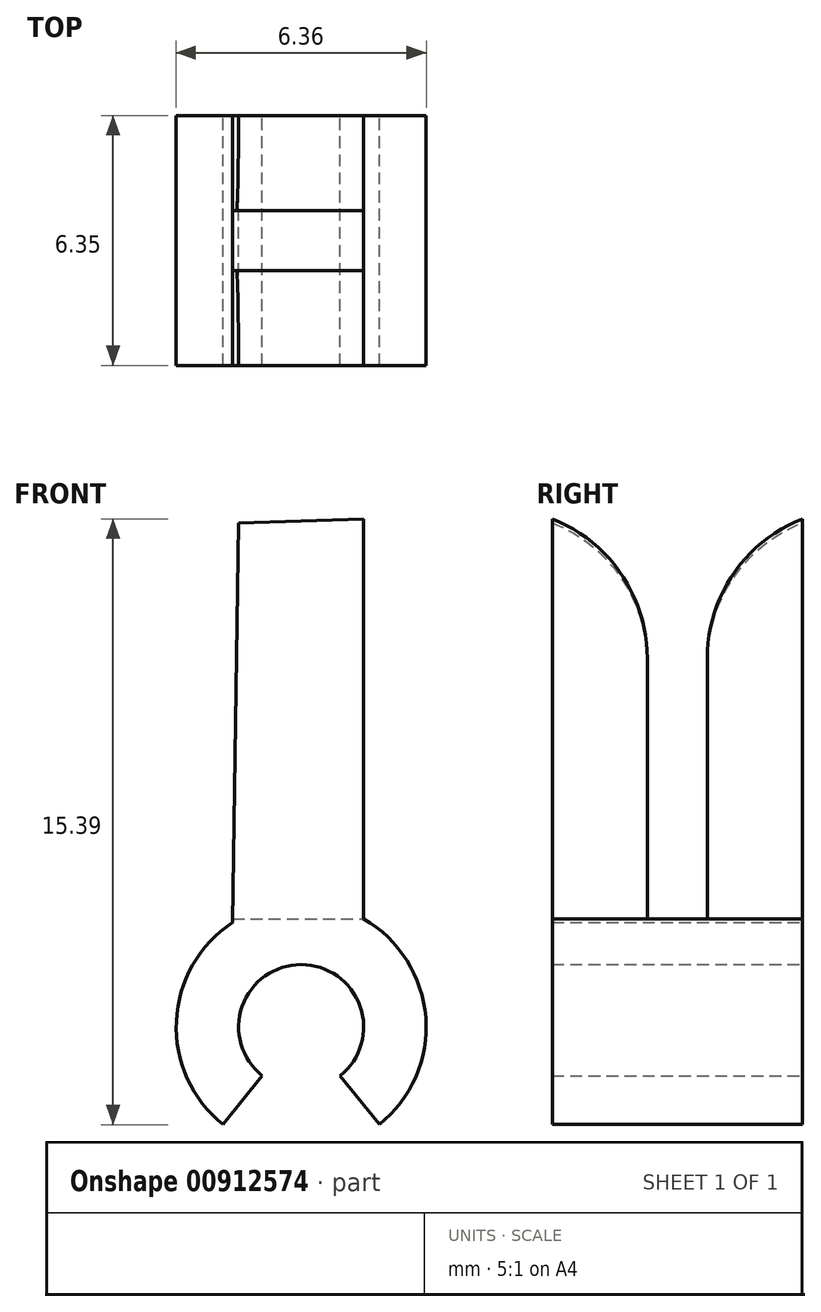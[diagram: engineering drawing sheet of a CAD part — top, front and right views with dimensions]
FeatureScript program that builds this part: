
annotation { "Feature Type Name" : "Feature", "Feature Type Description" : "" }
export const myFeature = defineFeature(function(context is Context, id is Id, definition is map)
    precondition{}
    {
        {
            var Q0;
            Q0=qCreatedBy(makeId("Front.planeOp"),FACE);
            var sketch = newSketch(context, id + "F0", { "sketchPlane" : qUnion([Q0])});
            skArc(sketch, "E0", {"start": v(1.99, -2.48) * mm, "mid": v(3.17, 0.24) * mm, "end": v(1.59, 2.75) * mm});
            skArc(sketch, "E1", {"start": v(1, -1.24) * mm, "mid": v(0, 1.59) * mm, "end": v(-1, -1.24) * mm});
            skLineSegment(sketch, "E2", {"start": v(-1, -1.24) * mm, "end": v(-1.99, -2.48) * mm});
            skLineSegment(sketch, "E3", {"start": v(1, -1.24) * mm, "end": v(1.99, -2.48) * mm});
            skArc(sketch, "E4.trimOffspring", {"start": v(-1.74, 2.65) * mm, "mid": v(-3.17, 0.15) * mm, "end": v(-1.99, -2.48) * mm});
            skLineSegment(sketch, "E5.left", {"start": v(-1.74, 2.65) * mm, "end": v(-1.59, 12.81) * mm});
            skLineSegment(sketch, "E6", {"start": v(-1.59, 12.81) * mm, "end": v(1.59, 12.9) * mm});
            skLineSegment(sketch, "E7", {"start": v(1.59, 12.9) * mm, "end": v(1.59, 2.75) * mm});
            skSolve(sketch);
        }
        {
            var Q0;
            Q0=makeQuery(id+"F0.imprint","IMPRINT",FACE,{"disambiguationData":[TD([[makeQuery(id+"F0.imprint","IMPRINT",EDGE,{"derivedFrom":sQuery(id+"F0.wireOp",EDGE,"E0")}),1.0]])]});
            extrude(context, id + "F1", {"entities" : qUnion([Q0]), "depth" : 6.35 * mm, "offsetDistance" : 25.4 * mm});
        }
        {
            var Q0;
            Q0=makeQuery(id+"F1.opExtrude","SWEPT_FACE",FACE,{"disambiguationData":[OSD([sQuery(id+"F0.wireOp",EDGE,"E7")])]});
            var sketch = newSketch(context, id + "F2", { "sketchPlane" : qUnion([Q0])});
            skLineSegment(sketch, "E8.bottom", {"start": v(-3.94, 12.9) * mm, "end": v(-2.41, 12.9) * mm});
            skLineSegment(sketch, "E8.top", {"start": v(-3.94, 2.75) * mm, "end": v(-2.41, 2.75) * mm});
            skLineSegment(sketch, "E8.left", {"start": v(-3.94, 12.9) * mm, "end": v(-3.94, 2.75) * mm});
            skLineSegment(sketch, "E8.right", {"start": v(-2.41, 12.9) * mm, "end": v(-2.41, 2.75) * mm});
            skSolve(sketch);
        }
        {
            var Q0;
            Q0=makeQuery(id+"F2.imprint","IMPRINT",FACE,{"disambiguationData":[TD([[makeQuery(id+"F2.imprint","IMPRINT",EDGE,{"derivedFrom":sQuery(id+"F2.wireOp",EDGE,"E8.bottom")}),-1.0]])]});
            extrude(context, id + "F3", {"entities" : qUnion([Q0]), "operationType" : NewBodyOperationType.REMOVE, "oppositeDirection" : true, "depth" : 25.4 * mm, "offsetDistance" : 25.4 * mm});
        }
        {
            var Q0;
            Q0=makeQuery(id+"F3.boolean.opBoolean","INTERSECT",EDGE,{"derivedFrom":[makeQuery(id+"F1.opExtrude","SWEPT_FACE",FACE,{"disambiguationData":[OSD([sQuery(id+"F0.wireOp",EDGE,"E6")])]}),makeQuery(id+"F3.opExtrude","SWEPT_FACE",FACE,{"disambiguationData":[OSD([sQuery(id+"F2.wireOp",EDGE,"E8.left")])]})]});
            fillet(context, id + "F4", {"entities" : qUnion([Q0]), "radius" : 3.8 * mm, "tangentPropagation" : true, "allowEdgeOverflow" : false});
        }
        {
            var Q0;
            Q0=makeQuery(id+"F3.boolean.opBoolean","INTERSECT",EDGE,{"derivedFrom":[makeQuery(id+"F1.opExtrude","SWEPT_FACE",FACE,{"disambiguationData":[OSD([sQuery(id+"F0.wireOp",EDGE,"E6")])]}),makeQuery(id+"F3.opExtrude","SWEPT_FACE",FACE,{"disambiguationData":[OSD([sQuery(id+"F2.wireOp",EDGE,"E8.right")])]})]});
            fillet(context, id + "F5", {"entities" : qUnion([Q0]), "radius" : 3.8 * mm, "tangentPropagation" : true, "allowEdgeOverflow" : false});
        }
    });
